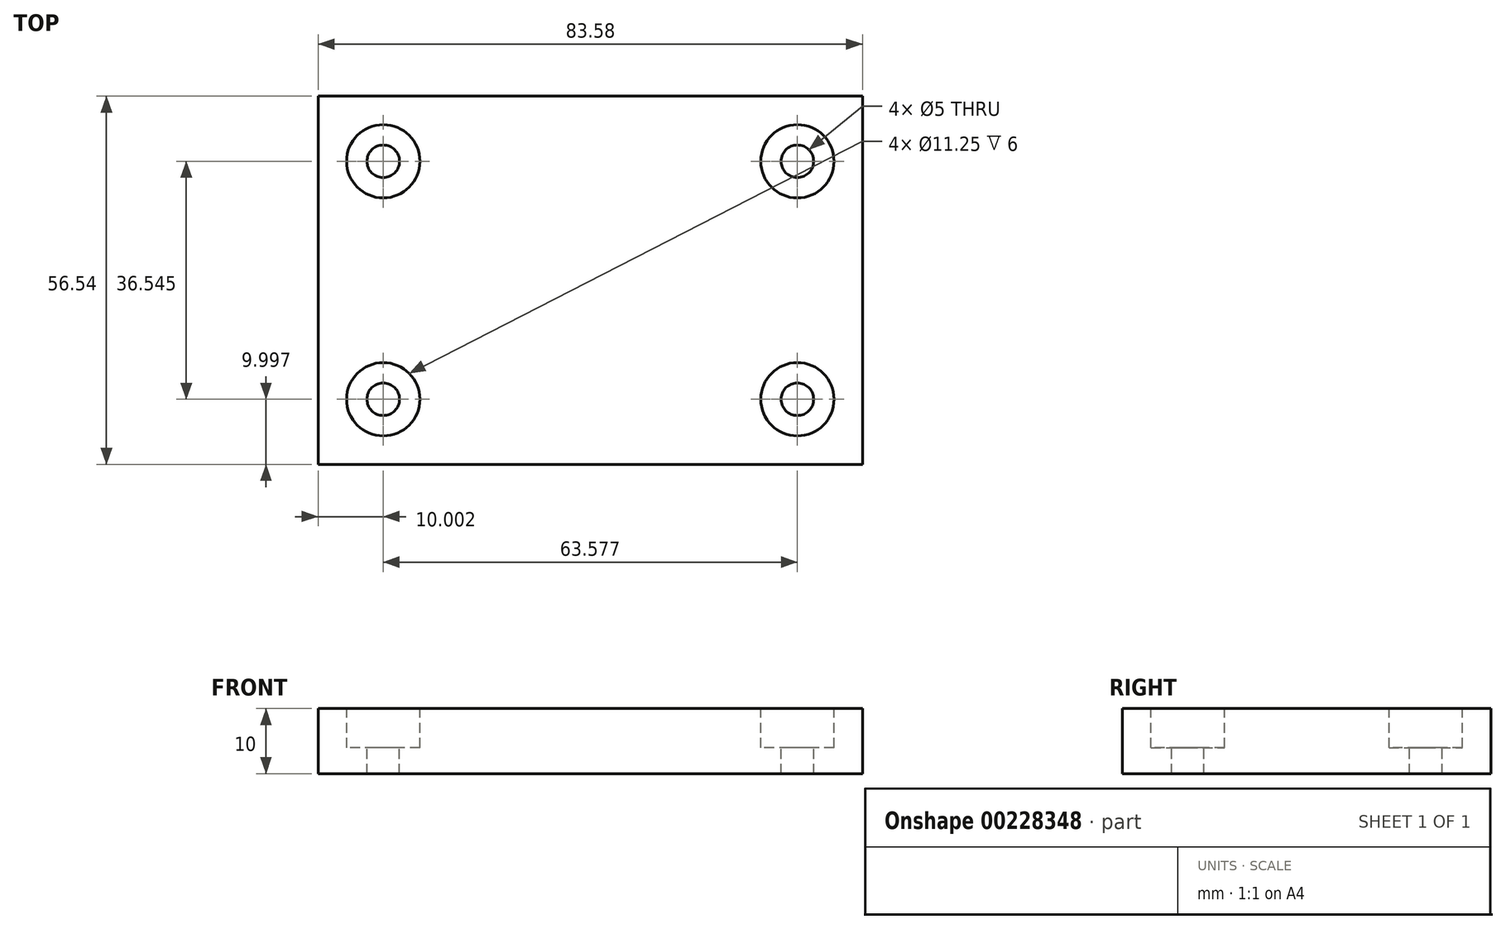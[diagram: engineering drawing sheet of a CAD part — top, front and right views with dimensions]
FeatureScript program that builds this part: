
annotation { "Feature Type Name" : "Feature", "Feature Type Description" : "" }
export const myFeature = defineFeature(function(context is Context, id is Id, definition is map)
    precondition{}
    {
        {
            var Q0;
            Q0=qCreatedBy(makeId("Top.planeOp"),FACE);
            var sketch = newSketch(context, id + "F0", { "sketchPlane" : qUnion([Q0])});
            skLineSegment(sketch, "E0.bottom", {"start": v(-41.79, -28.27) * mm, "end": v(41.79, -28.27) * mm});
            skLineSegment(sketch, "E0.top", {"start": v(-41.79, 28.27) * mm, "end": v(41.79, 28.27) * mm});
            skLineSegment(sketch, "E0.left", {"start": v(-41.79, -28.27) * mm, "end": v(-41.79, 28.27) * mm});
            skLineSegment(sketch, "E0.right", {"start": v(41.79, -28.27) * mm, "end": v(41.79, 28.27) * mm});
            skPoint(sketch, "E0.middle", {"position": v(0, 0) * mm});
            skSolve(sketch);
        }
        {
            var Q0;
            Q0=makeQuery(id+"F0.imprint","IMPRINT",FACE,{"disambiguationData":[TD([[makeQuery(id+"F0.imprint","IMPRINT",EDGE,{"derivedFrom":sQuery(id+"F0.wireOp",EDGE,"E0.bottom")}),1.0]])]});
            extrude(context, id + "F1", {"entities" : qUnion([Q0]), "depth" : 10 * mm});
        }
        {
            var Q0;
            Q0=makeQuery(id+"F1.opExtrude","CAP_FACE",FACE,{"disambiguationData":[OSD([sQuery(id+"F0.wireOp",EDGE,"E0.bottom"),sQuery(id+"F0.wireOp",EDGE,"E0.top"),sQuery(id+"F0.wireOp",EDGE,"E0.left"),sQuery(id+"F0.wireOp",EDGE,"E0.right")])],"isStart":false});
            var sketch = newSketch(context, id + "F2", { "sketchPlane" : qUnion([Q0])});
            skPoint(sketch, "E1", {"position": v(31.79, 18.27) * mm});
            skPoint(sketch, "E2.MirrorP", {"position": v(31.79, -18.27) * mm});
            skLineSegment(sketch, "E3", {"start": v(0, 28.27) * mm, "end": v(0, -28.27) * mm});
            skPoint(sketch, "E4.MirrorP", {"position": v(-31.79, 18.27) * mm});
            skPoint(sketch, "E5.MirrorP", {"position": v(-31.79, -18.27) * mm});
            skSolve(sketch);
        }
        {
            var Q0;
            Q0=sQuery(id+"F2.wireOp",VERTEX,"E4.MirrorP");
            var Q1;
            Q1=sQuery(id+"F2.wireOp",VERTEX,"E1");
            var Q2;
            Q2=sQuery(id+"F2.wireOp",VERTEX,"E2.MirrorP");
            var Q3;
            Q3=sQuery(id+"F2.wireOp",VERTEX,"E5.MirrorP");
            var Q4;
            Q4=makeQuery(id+"F1.opExtrude","SWEPT_BODY",BODY,{"disambiguationData":[OSD([sQuery(id+"F0.wireOp",EDGE,"E0.bottom"),sQuery(id+"F0.wireOp",EDGE,"E0.top"),sQuery(id+"F0.wireOp",EDGE,"E0.left"),sQuery(id+"F0.wireOp",EDGE,"E0.right")])]});
            hole(context, id + "F3", {"style" : HoleStyle.C_BORE, "endStyle" : HoleEndStyle.THROUGH, "standardTappedOrClearance" : lookupTablePath({ "standard" : "ISO", "engagement" : "75%", "pitch" : "1 mm", "size" : "M6", "type" : "Tapped" }), "standardBlindInLast" : lookupTablePath({ "standard" : "ISO", "engagement" : "75%", "pitch" : "1 mm", "size" : "M6", "type" : "Tapped" }), "holeDiameter" : 5 * mm, "cBoreDiameter" : 11.25 * mm, "cBoreDepth" : 6 * mm, "startFromSketch" : true, "locations" : qUnion([Q0, Q1, Q2, Q3]), "scope" : qUnion([Q4]), "isTappedThrough" : true, "majorDiameter" : 6 * mm, "showTappedDepth" : true});
        }
    });
